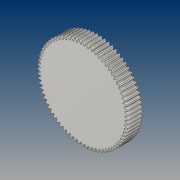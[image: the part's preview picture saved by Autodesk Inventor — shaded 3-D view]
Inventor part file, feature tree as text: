
AUTODESK INVENTOR PART (.ipt)
format: ipt  version: 2021 (Build 250183000, 183)  size: 412,672 bytes
history: native  units: mm (DEFAULTED — no unit token found)
features: plane x3, other x3, sketch x2, extrude x1
ambient origin geometry x8: Origin, YZ Plane, XZ Plane, XY Plane, X Axis, Y Axis, Z Axis, Center Point
bodies: Solid1 (feature_tree)
feature tree (9):
  extrude  "Extrusion1"  Depth=15.0mm TaperAngle=0.0deg
  plane  "Work Plane2"
  plane  "Work Plane8"
  plane  "Work Plane9"
  other  "Spur Gear"
  sketch  "Sketch1"  dims[d0=92.5mm d1=15.0mm d2=0.0mm]
  sketch  "Sketch2"  dims[d3=90.0mm d4=10.0mm d5=0.0mm d16=56.25mm d17=0.0mm d34=0.436332mm d39=0.0mm d41=0.0mm d43=56.25mm d46=56.25mm d47=0.0mm d48=0.0mm]
  other  "Srf1"
  other  "Pitch Diameter"
